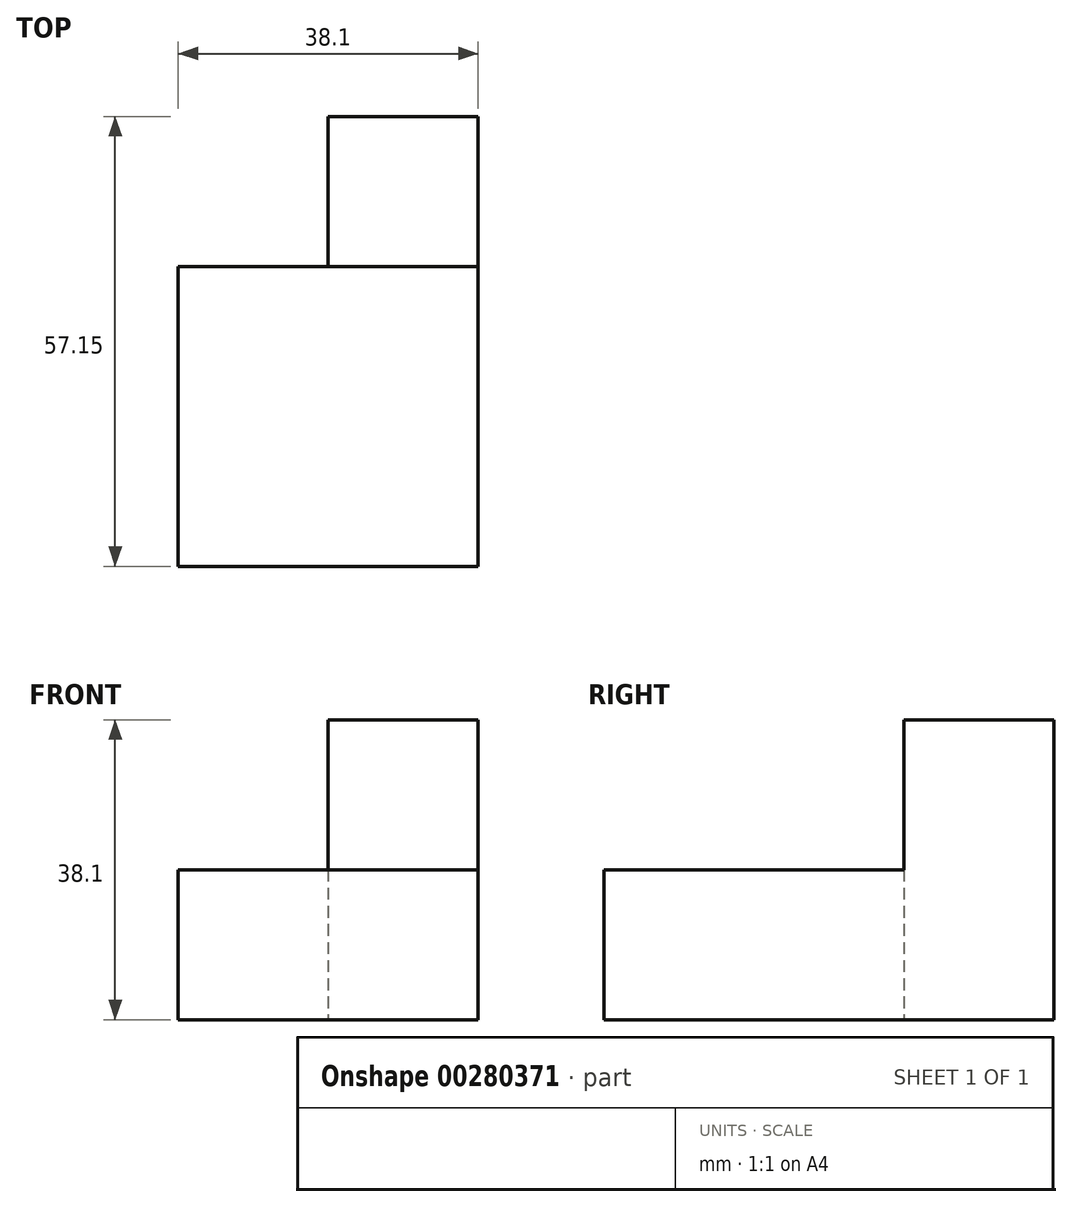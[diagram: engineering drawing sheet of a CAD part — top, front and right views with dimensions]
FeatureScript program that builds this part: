
annotation { "Feature Type Name" : "Feature", "Feature Type Description" : "" }
export const myFeature = defineFeature(function(context is Context, id is Id, definition is map)
    precondition{}
    {
        {
            var Q0;
            Q0=qCreatedBy(makeId("Top.planeOp"),FACE);
            var sketch = newSketch(context, id + "F0", { "sketchPlane" : qUnion([Q0])});
            skLineSegment(sketch, "E0.bottom", {"start": v(0, 38.1) * mm, "end": v(19.05, 38.1) * mm});
            skLineSegment(sketch, "E0.top", {"start": v(0, 0) * mm, "end": v(38.1, 0) * mm});
            skLineSegment(sketch, "E0.left", {"start": v(0, 38.1) * mm, "end": v(0, 0) * mm});
            skLineSegment(sketch, "E0.right", {"start": v(38.1, 38.1) * mm, "end": v(38.1, 0) * mm});
            skLineSegment(sketch, "E1.top", {"start": v(19.05, 57.15) * mm, "end": v(38.1, 57.15) * mm});
            skLineSegment(sketch, "E1.left", {"start": v(19.05, 38.1) * mm, "end": v(19.05, 57.15) * mm});
            skLineSegment(sketch, "E1.right", {"start": v(38.1, 38.1) * mm, "end": v(38.1, 57.15) * mm});
            skSolve(sketch);
        }
        {
            var Q0;
            Q0 = qSketchRegion(id + "F0", true);
            extrude(context, id + "F1", {"entities" : qUnion([Q0]), "depth" : 19.05 * mm});
        }
        {
            var Q0;
            Q0=makeQuery(id+"F1.opExtrude","CAP_FACE",FACE,{"disambiguationData":[OSD([sQuery(id+"F0.wireOp",EDGE,"E0.bottom"),sQuery(id+"F0.wireOp",EDGE,"E0.top"),sQuery(id+"F0.wireOp",EDGE,"E0.left"),sQuery(id+"F0.wireOp",EDGE,"E0.right"),sQuery(id+"F0.wireOp",EDGE,"E1.top"),sQuery(id+"F0.wireOp",EDGE,"E1.left"),sQuery(id+"F0.wireOp",EDGE,"E1.right")])],"isStart":false});
            var sketch = newSketch(context, id + "F2", { "sketchPlane" : qUnion([Q0])});
            skLineSegment(sketch, "E2.bottom", {"start": v(19.05, 57.15) * mm, "end": v(38.1, 57.15) * mm});
            skLineSegment(sketch, "E2.top", {"start": v(19.05, 38.1) * mm, "end": v(38.1, 38.1) * mm});
            skLineSegment(sketch, "E2.left", {"start": v(19.05, 57.15) * mm, "end": v(19.05, 38.1) * mm});
            skLineSegment(sketch, "E2.right", {"start": v(38.1, 57.15) * mm, "end": v(38.1, 38.1) * mm});
            skSolve(sketch);
        }
        {
            var Q0;
            Q0 = qSketchRegion(id + "F2", true);
            extrude(context, id + "F3", {"entities" : qUnion([Q0]), "operationType" : NewBodyOperationType.ADD, "depth" : 19.05 * mm});
        }
    });
